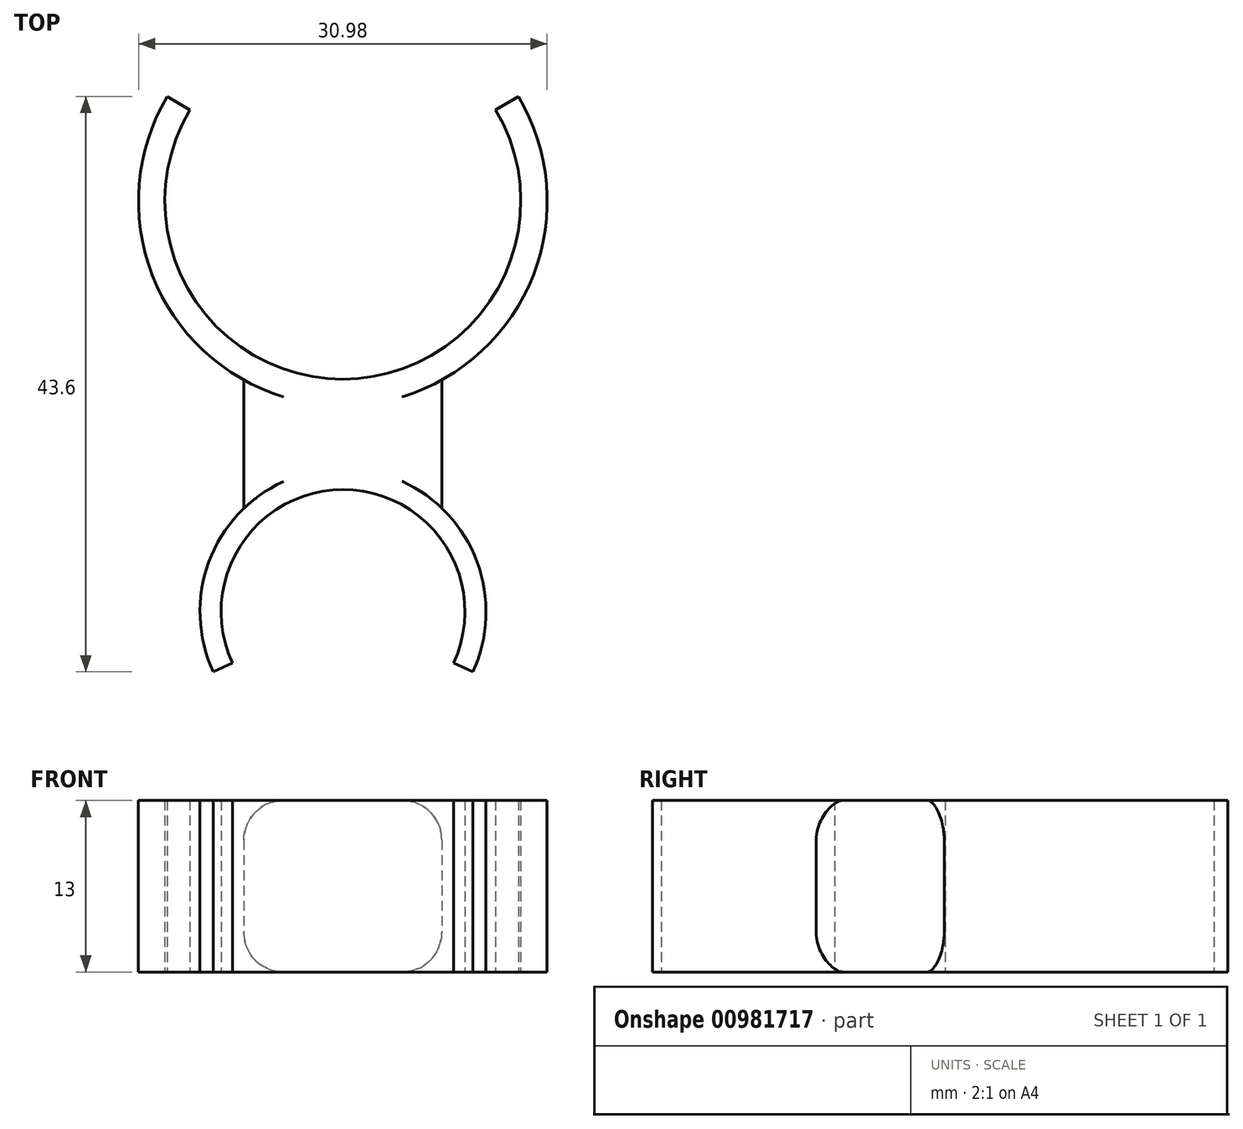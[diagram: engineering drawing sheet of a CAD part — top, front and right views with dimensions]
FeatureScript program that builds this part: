
annotation { "Feature Type Name" : "Feature", "Feature Type Description" : "" }
export const myFeature = defineFeature(function(context is Context, id is Id, definition is map)
    precondition{}
    {
        {
            var Q0;
            Q0=qCreatedBy(makeId("Top.planeOp"),FACE);
            var sketch = newSketch(context, id + "F0", { "sketchPlane" : qUnion([Q0])});
            skLineSegment(sketch, "E0", {"start": v(-21.36, 26.81) * mm, "end": v(23.86, 26.81) * mm, "construction": true});
            skPoint(sketch, "E1", {"position": v(-11.6, 26.81) * mm});
            skPoint(sketch, "E2", {"position": v(11.6, 26.81) * mm});
            skArc(sketch, "E3", {"start": v(-11.6, 26.81) * mm, "mid": v(0, 6.4) * mm, "end": v(11.6, 26.81) * mm});
            skArc(sketch, "E4.0", {"start": v(-13.3, 27.83) * mm, "mid": v(0, 4.4) * mm, "end": v(13.3, 27.83) * mm});
            skLineSegment(sketch, "E5", {"start": v(-13.3, 27.83) * mm, "end": v(-11.6, 26.81) * mm});
            skLineSegment(sketch, "E6", {"start": v(11.6, 26.81) * mm, "end": v(13.3, 27.83) * mm});
            skLineSegment(sketch, "E7", {"start": v(0, 19.9) * mm, "end": v(0, -19.01) * mm, "construction": true});
            skLineSegment(sketch, "E8", {"start": v(-8.37, -15.1) * mm, "end": v(8.4, -15.1) * mm, "construction": true});
            skArc(sketch, "E9", {"start": v(8.4, -15.1) * mm, "mid": v(0.01, -1.97) * mm, "end": v(-8.37, -15.1) * mm});
            skArc(sketch, "E10.0", {"start": v(9.85, -15.77) * mm, "mid": v(0.01, -0.37) * mm, "end": v(-9.83, -15.77) * mm});
            skLineSegment(sketch, "E11", {"start": v(-9.83, -15.77) * mm, "end": v(-8.37, -15.1) * mm});
            skLineSegment(sketch, "E12", {"start": v(8.4, -15.1) * mm, "end": v(9.85, -15.77) * mm});
            skLineSegment(sketch, "E13", {"start": v(-7.5, -3.4) * mm, "end": v(-7.5, 6.34) * mm});
            skLineSegment(sketch, "E14", {"start": v(7.5, -3.36) * mm, "end": v(7.5, 6.34) * mm});
            skSolve(sketch);
        }
        {
            var Q0;
            Q0 = qSketchRegion(id + "F0", true);
            extrude(context, id + "F1", {"entities" : qUnion([Q0]), "depth" : 13 * mm, "offsetDistance" : 25 * mm});
        }
        {
            var Q0;
            Q0=makeQuery(id+"F1.opExtrude","CAP_EDGE",EDGE,{"disambiguationData":[OSD([sQuery(id+"F0.wireOp",EDGE,"E14")])],"isStart":false});
            var Q1;
            Q1=makeQuery(id+"F1.opExtrude","CAP_EDGE",EDGE,{"disambiguationData":[OSD([sQuery(id+"F0.wireOp",EDGE,"E13")])],"isStart":false});
            var Q2;
            Q2=makeQuery(id+"F1.opExtrude","CAP_EDGE",EDGE,{"disambiguationData":[OSD([sQuery(id+"F0.wireOp",EDGE,"E14")])],"isStart":true});
            var Q3;
            Q3=makeQuery(id+"F1.opExtrude","CAP_EDGE",EDGE,{"disambiguationData":[OSD([sQuery(id+"F0.wireOp",EDGE,"E13")])],"isStart":true});
            fillet(context, id + "F2", {"entities" : qUnion([Q0, Q1, Q2, Q3]), "radius" : 3 * mm, "tangentPropagation" : true, "allowEdgeOverflow" : false});
        }
    });
